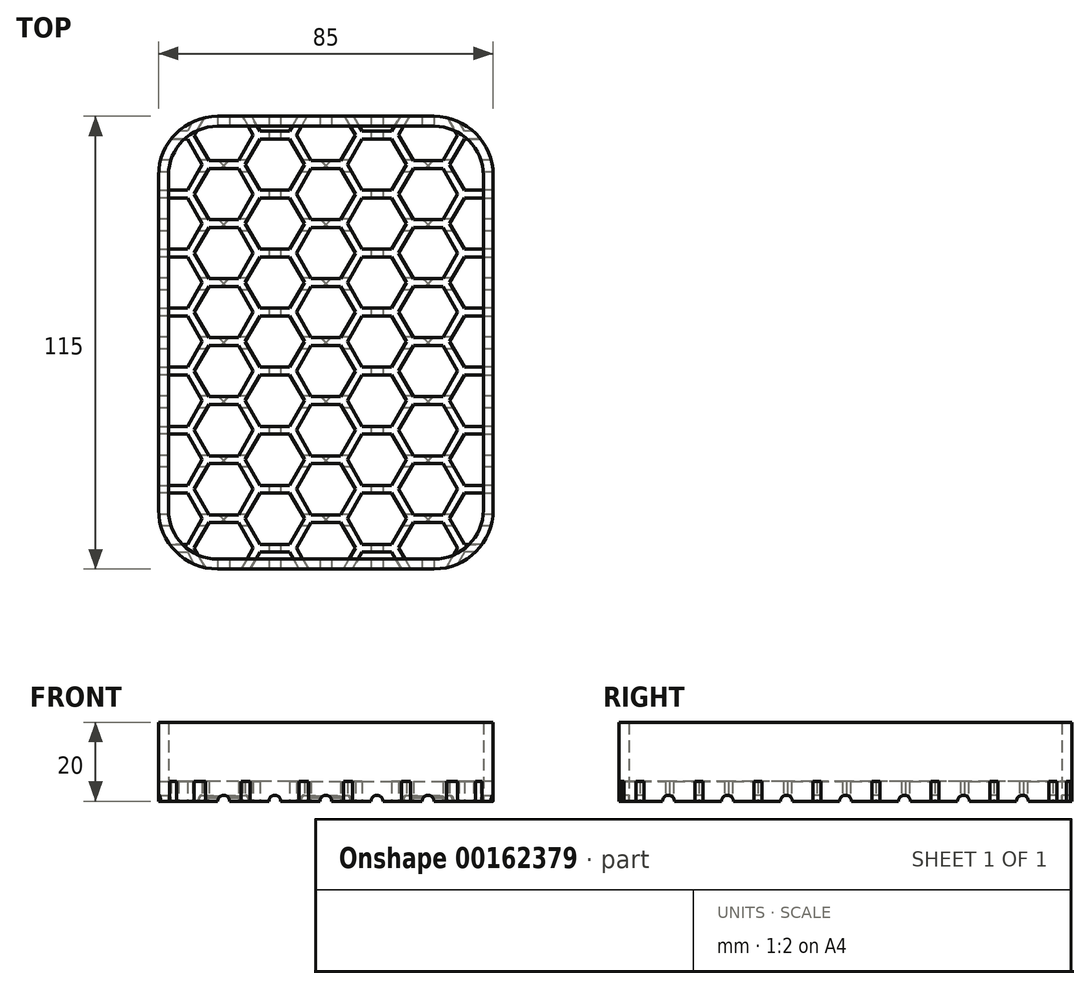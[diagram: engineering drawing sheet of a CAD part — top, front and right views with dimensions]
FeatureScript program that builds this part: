
annotation { "Feature Type Name" : "Feature", "Feature Type Description" : "" }
export const myFeature = defineFeature(function(context is Context, id is Id, definition is map)
    precondition{}
    {
        {
            var Q0;
            Q0=qCreatedBy(makeId("Top.planeOp"),FACE);
            var sketch = newSketch(context, id + "F0", { "sketchPlane" : qUnion([Q0])});
            skLineSegment(sketch, "E0.bottom", {"start": v(27.5, 57.5) * mm, "end": v(-27.5, 57.5) * mm});
            skLineSegment(sketch, "E0.top", {"start": v(27.5, -57.5) * mm, "end": v(-27.5, -57.5) * mm});
            skLineSegment(sketch, "E0.left", {"start": v(42.5, 42.5) * mm, "end": v(42.5, -42.5) * mm});
            skLineSegment(sketch, "E0.right", {"start": v(-42.5, 42.5) * mm, "end": v(-42.5, -42.5) * mm});
            skPoint(sketch, "E0.middle", {"position": v(0, 0) * mm});
            skArc(sketch, "E1", {"start": v(-27.5, 57.5) * mm, "mid": v(-38.1, 53.1) * mm, "end": v(-42.5, 42.5) * mm});
            skArc(sketch, "E2", {"start": v(42.5, 42.5) * mm, "mid": v(38.1, 53.1) * mm, "end": v(27.5, 57.5) * mm});
            skArc(sketch, "E3", {"start": v(27.5, -57.5) * mm, "mid": v(38.1, -53.1) * mm, "end": v(42.5, -42.5) * mm});
            skArc(sketch, "E4", {"start": v(-42.5, -42.5) * mm, "mid": v(-38.1, -53.1) * mm, "end": v(-27.5, -57.5) * mm});
            skSolve(sketch);
        }
        {
            var Q0;
            Q0=makeQuery(id+"F0.imprint","IMPRINT",FACE,{"disambiguationData":[TD([[makeQuery(id+"F0.imprint","IMPRINT",EDGE,{"derivedFrom":sQuery(id+"F0.wireOp",EDGE,"E0.bottom")}),1.0]])]});
            extrude(context, id + "F1", {"entities" : qUnion([Q0]), "depth" : 5 * mm});
        }
        {
            var Q0;
            Q0=qCreatedBy(makeId("Top.planeOp"),FACE);
            var sketch = newSketch(context, id + "F2", { "sketchPlane" : qUnion([Q0])});
            skCircle(sketch, "E5.cCircle", {"center": v(0, -52.22) * mm, "radius": 7.5 * mm, "construction": true});
            skLineSegment(sketch, "E5.0", {"start": v(7.5, -52.22) * mm, "end": v(3.75, -58.72) * mm});
            skLineSegment(sketch, "E5.1", {"start": v(3.75, -58.72) * mm, "end": v(-3.75, -58.72) * mm});
            skLineSegment(sketch, "E5.2", {"start": v(-3.75, -58.72) * mm, "end": v(-7.5, -52.22) * mm});
            skLineSegment(sketch, "E5.3", {"start": v(-7.5, -52.22) * mm, "end": v(-3.75, -45.73) * mm});
            skLineSegment(sketch, "E5.4", {"start": v(-3.75, -45.73) * mm, "end": v(3.75, -45.73) * mm});
            skLineSegment(sketch, "E5.5", {"start": v(3.75, -45.73) * mm, "end": v(7.5, -52.22) * mm});
            skCircle(sketch, "E6.cCircle", {"center": v(-12.98, -59.72) * mm, "radius": 7.5 * mm, "construction": true});
            skLineSegment(sketch, "E6.0", {"start": v(-16.73, -53.22) * mm, "end": v(-9.23, -53.22) * mm});
            skLineSegment(sketch, "E6.1", {"start": v(-9.23, -53.22) * mm, "end": v(-5.48, -59.72) * mm});
            skLineSegment(sketch, "E6.2", {"start": v(-5.48, -59.72) * mm, "end": v(-9.23, -66.21) * mm});
            skLineSegment(sketch, "E6.3", {"start": v(-9.23, -66.21) * mm, "end": v(-16.73, -66.21) * mm});
            skLineSegment(sketch, "E6.4", {"start": v(-16.73, -66.21) * mm, "end": v(-20.48, -59.72) * mm});
            skLineSegment(sketch, "E6.5", {"start": v(-20.48, -59.72) * mm, "end": v(-16.73, -53.22) * mm});
            skLineSegment(sketch, "E7", {"start": v(-12.98, -59.72) * mm, "end": v(0, -52.22) * mm, "construction": true});
            skCircle(sketch, "E8.MirrorC", {"center": v(12.98, -59.72) * mm, "radius": 7.5 * mm, "construction": true});
            skLineSegment(sketch, "E9.MirrorCS", {"start": v(5.48, -59.72) * mm, "end": v(9.23, -66.21) * mm});
            skLineSegment(sketch, "E10.MirrorCS", {"start": v(9.23, -66.21) * mm, "end": v(16.73, -66.21) * mm});
            skLineSegment(sketch, "E11.MirrorCS", {"start": v(16.73, -66.21) * mm, "end": v(20.48, -59.72) * mm});
            skLineSegment(sketch, "E12.MirrorCS", {"start": v(20.48, -59.72) * mm, "end": v(16.73, -53.22) * mm});
            skLineSegment(sketch, "E13.MirrorCS", {"start": v(16.73, -53.22) * mm, "end": v(9.23, -53.22) * mm});
            skLineSegment(sketch, "E14.MirrorCS", {"start": v(9.23, -53.22) * mm, "end": v(5.48, -59.72) * mm});
            skLineSegment(sketch, "E15.MirrorCS", {"start": v(12.98, -59.72) * mm, "end": v(0, -52.22) * mm, "construction": true});
            skLineSegment(sketch, "E16.1.0.0", {"start": v(38.95, -59.72) * mm, "end": v(25.96, -52.22) * mm, "construction": true});
            skLineSegment(sketch, "E16.1.0.1", {"start": v(29.71, -45.73) * mm, "end": v(33.46, -52.22) * mm});
            skLineSegment(sketch, "E16.1.0.2", {"start": v(12.98, -59.72) * mm, "end": v(25.96, -52.22) * mm, "construction": true});
            skLineSegment(sketch, "E16.1.0.3", {"start": v(22.21, -45.73) * mm, "end": v(29.71, -45.73) * mm});
            skLineSegment(sketch, "E16.1.0.4", {"start": v(42.7, -66.21) * mm, "end": v(46.45, -59.72) * mm});
            skLineSegment(sketch, "E16.1.0.5", {"start": v(46.45, -59.72) * mm, "end": v(42.7, -53.22) * mm});
            skLineSegment(sketch, "E16.1.0.6", {"start": v(31.45, -59.72) * mm, "end": v(35.2, -66.21) * mm});
            skCircle(sketch, "E16.1.0.7", {"center": v(25.96, -52.22) * mm, "radius": 7.5 * mm, "construction": true});
            skLineSegment(sketch, "E16.1.0.8", {"start": v(35.2, -53.22) * mm, "end": v(31.45, -59.72) * mm});
            skLineSegment(sketch, "E16.1.0.9", {"start": v(33.46, -52.22) * mm, "end": v(29.71, -58.72) * mm});
            skLineSegment(sketch, "E16.1.0.10", {"start": v(35.2, -66.21) * mm, "end": v(42.7, -66.21) * mm});
            skLineSegment(sketch, "E16.1.0.11", {"start": v(29.71, -58.72) * mm, "end": v(22.21, -58.72) * mm});
            skLineSegment(sketch, "E16.1.0.12", {"start": v(22.21, -58.72) * mm, "end": v(18.46, -52.22) * mm});
            skLineSegment(sketch, "E16.1.0.13", {"start": v(42.7, -53.22) * mm, "end": v(35.2, -53.22) * mm});
            skLineSegment(sketch, "E16.1.0.14", {"start": v(18.46, -52.22) * mm, "end": v(22.21, -45.73) * mm});
            skCircle(sketch, "E16.1.0.15", {"center": v(38.95, -59.72) * mm, "radius": 7.5 * mm, "construction": true});
            skLineSegment(sketch, "E16.direction1", {"start": v(-12.98, -59.72) * mm, "end": v(12.98, -59.72) * mm, "construction": true});
            skCircle(sketch, "E17.MirrorC", {"center": v(-25.96, -52.22) * mm, "radius": 7.5 * mm, "construction": true});
            skLineSegment(sketch, "E18.MirrorCS", {"start": v(-35.2, -66.21) * mm, "end": v(-42.7, -66.21) * mm});
            skLineSegment(sketch, "E19.MirrorCS", {"start": v(-12.98, -59.72) * mm, "end": v(-25.96, -52.22) * mm, "construction": true});
            skLineSegment(sketch, "E20.MirrorCS", {"start": v(-38.95, -59.72) * mm, "end": v(-25.96, -52.22) * mm, "construction": true});
            skLineSegment(sketch, "E21.MirrorCS", {"start": v(-46.45, -59.72) * mm, "end": v(-42.7, -53.22) * mm});
            skCircle(sketch, "E22.MirrorC", {"center": v(-38.95, -59.72) * mm, "radius": 7.5 * mm, "construction": true});
            skLineSegment(sketch, "E23.MirrorCS", {"start": v(-35.2, -53.22) * mm, "end": v(-31.45, -59.72) * mm});
            skLineSegment(sketch, "E24.MirrorCS", {"start": v(-29.71, -58.72) * mm, "end": v(-22.21, -58.72) * mm});
            skLineSegment(sketch, "E25.MirrorCS", {"start": v(-22.21, -45.73) * mm, "end": v(-29.71, -45.73) * mm});
            skLineSegment(sketch, "E26.MirrorCS", {"start": v(-22.21, -58.72) * mm, "end": v(-18.46, -52.22) * mm});
            skLineSegment(sketch, "E27.MirrorCS", {"start": v(-18.46, -52.22) * mm, "end": v(-22.21, -45.73) * mm});
            skLineSegment(sketch, "E28.MirrorCS", {"start": v(-31.45, -59.72) * mm, "end": v(-35.2, -66.21) * mm});
            skLineSegment(sketch, "E29.MirrorCS", {"start": v(-42.7, -66.21) * mm, "end": v(-46.45, -59.72) * mm});
            skLineSegment(sketch, "E30.MirrorCS", {"start": v(-33.46, -52.22) * mm, "end": v(-29.71, -58.72) * mm});
            skLineSegment(sketch, "E31.MirrorCS", {"start": v(-29.71, -45.73) * mm, "end": v(-33.46, -52.22) * mm});
            skLineSegment(sketch, "E32.MirrorCS", {"start": v(-42.7, -53.22) * mm, "end": v(-35.2, -53.22) * mm});
            skLineSegment(sketch, "E33.0.1.0", {"start": v(-3.75, -30.74) * mm, "end": v(3.75, -30.74) * mm});
            skLineSegment(sketch, "E33.0.1.1", {"start": v(-7.5, -37.23) * mm, "end": v(-3.75, -30.74) * mm});
            skLineSegment(sketch, "E33.0.1.2", {"start": v(7.5, -37.23) * mm, "end": v(3.75, -43.73) * mm});
            skLineSegment(sketch, "E33.0.1.3", {"start": v(-20.48, -44.73) * mm, "end": v(-16.73, -38.23) * mm});
            skCircle(sketch, "E33.0.1.4", {"center": v(-25.96, -37.23) * mm, "radius": 7.5 * mm, "construction": true});
            skLineSegment(sketch, "E33.0.1.5", {"start": v(35.2, -38.23) * mm, "end": v(31.45, -44.73) * mm});
            skLineSegment(sketch, "E33.0.1.6", {"start": v(12.98, -44.73) * mm, "end": v(0, -37.23) * mm, "construction": true});
            skCircle(sketch, "E33.0.1.7", {"center": v(38.95, -44.73) * mm, "radius": 7.5 * mm, "construction": true});
            skLineSegment(sketch, "E33.0.1.8", {"start": v(-12.98, -44.73) * mm, "end": v(0, -37.23) * mm, "construction": true});
            skLineSegment(sketch, "E33.0.1.9", {"start": v(9.23, -38.23) * mm, "end": v(5.48, -44.73) * mm});
            skCircle(sketch, "E33.0.1.10", {"center": v(-38.95, -44.73) * mm, "radius": 7.5 * mm, "construction": true});
            skLineSegment(sketch, "E33.0.1.11", {"start": v(-5.48, -44.73) * mm, "end": v(-9.23, -51.22) * mm});
            skLineSegment(sketch, "E33.0.1.12", {"start": v(33.46, -37.23) * mm, "end": v(29.71, -43.73) * mm});
            skLineSegment(sketch, "E33.0.1.13", {"start": v(35.2, -51.22) * mm, "end": v(42.7, -51.22) * mm});
            skLineSegment(sketch, "E33.0.1.14", {"start": v(29.71, -43.73) * mm, "end": v(22.21, -43.73) * mm});
            skLineSegment(sketch, "E33.0.1.15", {"start": v(12.98, -44.73) * mm, "end": v(25.96, -37.23) * mm, "construction": true});
            skCircle(sketch, "E33.0.1.16", {"center": v(0, -37.23) * mm, "radius": 7.5 * mm, "construction": true});
            skCircle(sketch, "E33.0.1.17", {"center": v(-12.98, -44.73) * mm, "radius": 7.5 * mm, "construction": true});
            skLineSegment(sketch, "E33.0.1.18", {"start": v(-16.73, -38.23) * mm, "end": v(-9.23, -38.23) * mm});
            skLineSegment(sketch, "E33.0.1.19", {"start": v(-3.75, -43.73) * mm, "end": v(-7.5, -37.23) * mm});
            skLineSegment(sketch, "E33.0.1.20", {"start": v(3.75, -30.74) * mm, "end": v(7.5, -37.23) * mm});
            skLineSegment(sketch, "E33.0.1.21", {"start": v(-22.21, -43.73) * mm, "end": v(-18.46, -37.23) * mm});
            skLineSegment(sketch, "E33.0.1.22", {"start": v(-31.45, -44.73) * mm, "end": v(-35.2, -51.22) * mm});
            skLineSegment(sketch, "E33.0.1.23", {"start": v(16.73, -38.23) * mm, "end": v(9.23, -38.23) * mm});
            skLineSegment(sketch, "E33.0.1.24", {"start": v(29.71, -30.74) * mm, "end": v(33.46, -37.23) * mm});
            skLineSegment(sketch, "E33.0.1.25", {"start": v(46.45, -44.73) * mm, "end": v(42.7, -38.23) * mm});
            skLineSegment(sketch, "E33.0.1.26", {"start": v(42.7, -51.22) * mm, "end": v(46.45, -44.73) * mm});
            skLineSegment(sketch, "E33.0.1.27", {"start": v(5.48, -44.73) * mm, "end": v(9.23, -51.22) * mm});
            skLineSegment(sketch, "E33.0.1.28", {"start": v(-46.45, -44.73) * mm, "end": v(-42.7, -38.23) * mm});
            skLineSegment(sketch, "E33.0.1.29", {"start": v(31.45, -44.73) * mm, "end": v(35.2, -51.22) * mm});
            skLineSegment(sketch, "E33.0.1.30", {"start": v(16.73, -51.22) * mm, "end": v(20.48, -44.73) * mm});
            skLineSegment(sketch, "E33.0.1.31", {"start": v(-16.73, -51.22) * mm, "end": v(-20.48, -44.73) * mm});
            skLineSegment(sketch, "E33.0.1.32", {"start": v(-29.71, -43.73) * mm, "end": v(-22.21, -43.73) * mm});
            skLineSegment(sketch, "E33.0.1.33", {"start": v(20.48, -44.73) * mm, "end": v(16.73, -38.23) * mm});
            skLineSegment(sketch, "E33.0.1.34", {"start": v(-12.98, -44.73) * mm, "end": v(-25.96, -37.23) * mm, "construction": true});
            skLineSegment(sketch, "E33.0.1.35", {"start": v(-18.46, -37.23) * mm, "end": v(-22.21, -30.74) * mm});
            skLineSegment(sketch, "E33.0.1.36", {"start": v(42.7, -38.23) * mm, "end": v(35.2, -38.23) * mm});
            skLineSegment(sketch, "E33.0.1.37", {"start": v(-22.21, -30.74) * mm, "end": v(-29.71, -30.74) * mm});
            skLineSegment(sketch, "E33.0.1.38", {"start": v(-35.2, -38.23) * mm, "end": v(-31.45, -44.73) * mm});
            skLineSegment(sketch, "E33.0.1.39", {"start": v(-9.23, -51.22) * mm, "end": v(-16.73, -51.22) * mm});
            skLineSegment(sketch, "E33.0.1.40", {"start": v(22.21, -30.74) * mm, "end": v(29.71, -30.74) * mm});
            skLineSegment(sketch, "E33.0.1.41", {"start": v(22.21, -43.73) * mm, "end": v(18.46, -37.23) * mm});
            skLineSegment(sketch, "E33.0.1.42", {"start": v(3.75, -43.73) * mm, "end": v(-3.75, -43.73) * mm});
            skLineSegment(sketch, "E33.0.1.43", {"start": v(38.95, -44.73) * mm, "end": v(25.96, -37.23) * mm, "construction": true});
            skCircle(sketch, "E33.0.1.44", {"center": v(12.98, -44.73) * mm, "radius": 7.5 * mm, "construction": true});
            skLineSegment(sketch, "E33.0.1.45", {"start": v(-29.71, -30.74) * mm, "end": v(-33.46, -37.23) * mm});
            skCircle(sketch, "E33.0.1.46", {"center": v(25.96, -37.23) * mm, "radius": 7.5 * mm, "construction": true});
            skLineSegment(sketch, "E33.0.1.47", {"start": v(18.46, -37.23) * mm, "end": v(22.21, -30.74) * mm});
            skLineSegment(sketch, "E33.0.1.48", {"start": v(-35.2, -51.22) * mm, "end": v(-42.7, -51.22) * mm});
            skLineSegment(sketch, "E33.0.1.49", {"start": v(9.23, -51.22) * mm, "end": v(16.73, -51.22) * mm});
            skLineSegment(sketch, "E33.0.1.50", {"start": v(-33.46, -37.23) * mm, "end": v(-29.71, -43.73) * mm});
            skLineSegment(sketch, "E33.0.1.51", {"start": v(-42.7, -38.23) * mm, "end": v(-35.2, -38.23) * mm});
            skLineSegment(sketch, "E33.0.1.52", {"start": v(-42.7, -51.22) * mm, "end": v(-46.45, -44.73) * mm});
            skLineSegment(sketch, "E33.0.1.53", {"start": v(-38.95, -44.73) * mm, "end": v(-25.96, -37.23) * mm, "construction": true});
            skLineSegment(sketch, "E33.0.1.54", {"start": v(-12.98, -44.73) * mm, "end": v(12.98, -44.73) * mm, "construction": true});
            skLineSegment(sketch, "E33.0.1.55", {"start": v(-9.23, -38.23) * mm, "end": v(-5.48, -44.73) * mm});
            skLineSegment(sketch, "E33.0.2.0", {"start": v(-3.75, -15.75) * mm, "end": v(3.75, -15.75) * mm});
            skLineSegment(sketch, "E33.0.2.1", {"start": v(-7.5, -22.24) * mm, "end": v(-3.75, -15.75) * mm});
            skLineSegment(sketch, "E33.0.2.2", {"start": v(7.5, -22.24) * mm, "end": v(3.75, -28.74) * mm});
            skLineSegment(sketch, "E33.0.2.3", {"start": v(-20.48, -29.74) * mm, "end": v(-16.73, -23.24) * mm});
            skCircle(sketch, "E33.0.2.4", {"center": v(-25.96, -22.24) * mm, "radius": 7.5 * mm, "construction": true});
            skLineSegment(sketch, "E33.0.2.5", {"start": v(35.2, -23.24) * mm, "end": v(31.45, -29.74) * mm});
            skLineSegment(sketch, "E33.0.2.6", {"start": v(12.98, -29.74) * mm, "end": v(0, -22.24) * mm, "construction": true});
            skCircle(sketch, "E33.0.2.7", {"center": v(38.95, -29.74) * mm, "radius": 7.5 * mm, "construction": true});
            skLineSegment(sketch, "E33.0.2.8", {"start": v(-12.98, -29.74) * mm, "end": v(0, -22.24) * mm, "construction": true});
            skLineSegment(sketch, "E33.0.2.9", {"start": v(9.23, -23.24) * mm, "end": v(5.48, -29.74) * mm});
            skCircle(sketch, "E33.0.2.10", {"center": v(-38.95, -29.74) * mm, "radius": 7.5 * mm, "construction": true});
            skLineSegment(sketch, "E33.0.2.11", {"start": v(-5.48, -29.74) * mm, "end": v(-9.23, -36.23) * mm});
            skLineSegment(sketch, "E33.0.2.12", {"start": v(33.46, -22.24) * mm, "end": v(29.71, -28.74) * mm});
            skLineSegment(sketch, "E33.0.2.13", {"start": v(35.2, -36.23) * mm, "end": v(42.7, -36.23) * mm});
            skLineSegment(sketch, "E33.0.2.14", {"start": v(29.71, -28.74) * mm, "end": v(22.21, -28.74) * mm});
            skLineSegment(sketch, "E33.0.2.15", {"start": v(12.98, -29.74) * mm, "end": v(25.96, -22.24) * mm, "construction": true});
            skCircle(sketch, "E33.0.2.16", {"center": v(0, -22.24) * mm, "radius": 7.5 * mm, "construction": true});
            skCircle(sketch, "E33.0.2.17", {"center": v(-12.98, -29.74) * mm, "radius": 7.5 * mm, "construction": true});
            skLineSegment(sketch, "E33.0.2.18", {"start": v(-16.73, -23.24) * mm, "end": v(-9.23, -23.24) * mm});
            skLineSegment(sketch, "E33.0.2.19", {"start": v(-3.75, -28.74) * mm, "end": v(-7.5, -22.24) * mm});
            skLineSegment(sketch, "E33.0.2.20", {"start": v(3.75, -15.75) * mm, "end": v(7.5, -22.24) * mm});
            skLineSegment(sketch, "E33.0.2.21", {"start": v(-22.21, -28.74) * mm, "end": v(-18.46, -22.24) * mm});
            skLineSegment(sketch, "E33.0.2.22", {"start": v(-31.45, -29.74) * mm, "end": v(-35.2, -36.23) * mm});
            skLineSegment(sketch, "E33.0.2.23", {"start": v(16.73, -23.24) * mm, "end": v(9.23, -23.24) * mm});
            skLineSegment(sketch, "E33.0.2.24", {"start": v(29.71, -15.75) * mm, "end": v(33.46, -22.24) * mm});
            skLineSegment(sketch, "E33.0.2.25", {"start": v(46.45, -29.74) * mm, "end": v(42.7, -23.24) * mm});
            skLineSegment(sketch, "E33.0.2.26", {"start": v(42.7, -36.23) * mm, "end": v(46.45, -29.74) * mm});
            skLineSegment(sketch, "E33.0.2.27", {"start": v(5.48, -29.74) * mm, "end": v(9.23, -36.23) * mm});
            skLineSegment(sketch, "E33.0.2.28", {"start": v(-46.45, -29.74) * mm, "end": v(-42.7, -23.24) * mm});
            skLineSegment(sketch, "E33.0.2.29", {"start": v(31.45, -29.74) * mm, "end": v(35.2, -36.23) * mm});
            skLineSegment(sketch, "E33.0.2.30", {"start": v(16.73, -36.23) * mm, "end": v(20.48, -29.74) * mm});
            skLineSegment(sketch, "E33.0.2.31", {"start": v(-16.73, -36.23) * mm, "end": v(-20.48, -29.74) * mm});
            skLineSegment(sketch, "E33.0.2.32", {"start": v(-29.71, -28.74) * mm, "end": v(-22.21, -28.74) * mm});
            skLineSegment(sketch, "E33.0.2.33", {"start": v(20.48, -29.74) * mm, "end": v(16.73, -23.24) * mm});
            skLineSegment(sketch, "E33.0.2.34", {"start": v(-12.98, -29.74) * mm, "end": v(-25.96, -22.24) * mm, "construction": true});
            skLineSegment(sketch, "E33.0.2.35", {"start": v(-18.46, -22.24) * mm, "end": v(-22.21, -15.75) * mm});
            skLineSegment(sketch, "E33.0.2.36", {"start": v(42.7, -23.24) * mm, "end": v(35.2, -23.24) * mm});
            skLineSegment(sketch, "E33.0.2.37", {"start": v(-22.21, -15.75) * mm, "end": v(-29.71, -15.75) * mm});
            skLineSegment(sketch, "E33.0.2.38", {"start": v(-35.2, -23.24) * mm, "end": v(-31.45, -29.74) * mm});
            skLineSegment(sketch, "E33.0.2.39", {"start": v(-9.23, -36.23) * mm, "end": v(-16.73, -36.23) * mm});
            skLineSegment(sketch, "E33.0.2.40", {"start": v(22.21, -15.75) * mm, "end": v(29.71, -15.75) * mm});
            skLineSegment(sketch, "E33.0.2.41", {"start": v(22.21, -28.74) * mm, "end": v(18.46, -22.24) * mm});
            skLineSegment(sketch, "E33.0.2.42", {"start": v(3.75, -28.74) * mm, "end": v(-3.75, -28.74) * mm});
            skLineSegment(sketch, "E33.0.2.43", {"start": v(38.95, -29.74) * mm, "end": v(25.96, -22.24) * mm, "construction": true});
            skCircle(sketch, "E33.0.2.44", {"center": v(12.98, -29.74) * mm, "radius": 7.5 * mm, "construction": true});
            skLineSegment(sketch, "E33.0.2.45", {"start": v(-29.71, -15.75) * mm, "end": v(-33.46, -22.24) * mm});
            skCircle(sketch, "E33.0.2.46", {"center": v(25.96, -22.24) * mm, "radius": 7.5 * mm, "construction": true});
            skLineSegment(sketch, "E33.0.2.47", {"start": v(18.46, -22.24) * mm, "end": v(22.21, -15.75) * mm});
            skLineSegment(sketch, "E33.0.2.48", {"start": v(-35.2, -36.23) * mm, "end": v(-42.7, -36.23) * mm});
            skLineSegment(sketch, "E33.0.2.49", {"start": v(9.23, -36.23) * mm, "end": v(16.73, -36.23) * mm});
            skLineSegment(sketch, "E33.0.2.50", {"start": v(-33.46, -22.24) * mm, "end": v(-29.71, -28.74) * mm});
            skLineSegment(sketch, "E33.0.2.51", {"start": v(-42.7, -23.24) * mm, "end": v(-35.2, -23.24) * mm});
            skLineSegment(sketch, "E33.0.2.52", {"start": v(-42.7, -36.23) * mm, "end": v(-46.45, -29.74) * mm});
            skLineSegment(sketch, "E33.0.2.53", {"start": v(-38.95, -29.74) * mm, "end": v(-25.96, -22.24) * mm, "construction": true});
            skLineSegment(sketch, "E33.0.2.54", {"start": v(-12.98, -29.74) * mm, "end": v(12.98, -29.74) * mm, "construction": true});
            skLineSegment(sketch, "E33.0.2.55", {"start": v(-9.23, -23.24) * mm, "end": v(-5.48, -29.74) * mm});
            skLineSegment(sketch, "E33.0.3.0", {"start": v(-3.75, -0.76) * mm, "end": v(3.75, -0.76) * mm});
            skLineSegment(sketch, "E33.0.3.1", {"start": v(-7.5, -7.25) * mm, "end": v(-3.75, -0.76) * mm});
            skLineSegment(sketch, "E33.0.3.2", {"start": v(7.5, -7.25) * mm, "end": v(3.75, -13.75) * mm});
            skLineSegment(sketch, "E33.0.3.3", {"start": v(-20.48, -14.75) * mm, "end": v(-16.73, -8.25) * mm});
            skCircle(sketch, "E33.0.3.4", {"center": v(-25.96, -7.25) * mm, "radius": 7.5 * mm, "construction": true});
            skLineSegment(sketch, "E33.0.3.5", {"start": v(35.2, -8.25) * mm, "end": v(31.45, -14.75) * mm});
            skLineSegment(sketch, "E33.0.3.6", {"start": v(12.98, -14.75) * mm, "end": v(0, -7.25) * mm, "construction": true});
            skCircle(sketch, "E33.0.3.7", {"center": v(38.95, -14.75) * mm, "radius": 7.5 * mm, "construction": true});
            skLineSegment(sketch, "E33.0.3.8", {"start": v(-12.98, -14.75) * mm, "end": v(0, -7.25) * mm, "construction": true});
            skLineSegment(sketch, "E33.0.3.9", {"start": v(9.23, -8.25) * mm, "end": v(5.48, -14.75) * mm});
            skCircle(sketch, "E33.0.3.10", {"center": v(-38.95, -14.75) * mm, "radius": 7.5 * mm, "construction": true});
            skLineSegment(sketch, "E33.0.3.11", {"start": v(-5.48, -14.75) * mm, "end": v(-9.23, -21.24) * mm});
            skLineSegment(sketch, "E33.0.3.12", {"start": v(33.46, -7.25) * mm, "end": v(29.71, -13.75) * mm});
            skLineSegment(sketch, "E33.0.3.13", {"start": v(35.2, -21.24) * mm, "end": v(42.7, -21.24) * mm});
            skLineSegment(sketch, "E33.0.3.14", {"start": v(29.71, -13.75) * mm, "end": v(22.21, -13.75) * mm});
            skLineSegment(sketch, "E33.0.3.15", {"start": v(12.98, -14.75) * mm, "end": v(25.96, -7.25) * mm, "construction": true});
            skCircle(sketch, "E33.0.3.16", {"center": v(0, -7.25) * mm, "radius": 7.5 * mm, "construction": true});
            skCircle(sketch, "E33.0.3.17", {"center": v(-12.98, -14.75) * mm, "radius": 7.5 * mm, "construction": true});
            skLineSegment(sketch, "E33.0.3.18", {"start": v(-16.73, -8.25) * mm, "end": v(-9.23, -8.25) * mm});
            skLineSegment(sketch, "E33.0.3.19", {"start": v(-3.75, -13.75) * mm, "end": v(-7.5, -7.25) * mm});
            skLineSegment(sketch, "E33.0.3.20", {"start": v(3.75, -0.76) * mm, "end": v(7.5, -7.25) * mm});
            skLineSegment(sketch, "E33.0.3.21", {"start": v(-22.21, -13.75) * mm, "end": v(-18.46, -7.25) * mm});
            skLineSegment(sketch, "E33.0.3.22", {"start": v(-31.45, -14.75) * mm, "end": v(-35.2, -21.24) * mm});
            skLineSegment(sketch, "E33.0.3.23", {"start": v(16.73, -8.25) * mm, "end": v(9.23, -8.25) * mm});
            skLineSegment(sketch, "E33.0.3.24", {"start": v(29.71, -0.76) * mm, "end": v(33.46, -7.25) * mm});
            skLineSegment(sketch, "E33.0.3.25", {"start": v(46.45, -14.75) * mm, "end": v(42.7, -8.25) * mm});
            skLineSegment(sketch, "E33.0.3.26", {"start": v(42.7, -21.24) * mm, "end": v(46.45, -14.75) * mm});
            skLineSegment(sketch, "E33.0.3.27", {"start": v(5.48, -14.75) * mm, "end": v(9.23, -21.24) * mm});
            skLineSegment(sketch, "E33.0.3.28", {"start": v(-46.45, -14.75) * mm, "end": v(-42.7, -8.25) * mm});
            skLineSegment(sketch, "E33.0.3.29", {"start": v(31.45, -14.75) * mm, "end": v(35.2, -21.24) * mm});
            skLineSegment(sketch, "E33.0.3.30", {"start": v(16.73, -21.24) * mm, "end": v(20.48, -14.75) * mm});
            skLineSegment(sketch, "E33.0.3.31", {"start": v(-16.73, -21.24) * mm, "end": v(-20.48, -14.75) * mm});
            skLineSegment(sketch, "E33.0.3.32", {"start": v(-29.71, -13.75) * mm, "end": v(-22.21, -13.75) * mm});
            skLineSegment(sketch, "E33.0.3.33", {"start": v(20.48, -14.75) * mm, "end": v(16.73, -8.25) * mm});
            skLineSegment(sketch, "E33.0.3.34", {"start": v(-12.98, -14.75) * mm, "end": v(-25.96, -7.25) * mm, "construction": true});
            skLineSegment(sketch, "E33.0.3.35", {"start": v(-18.46, -7.25) * mm, "end": v(-22.21, -0.76) * mm});
            skLineSegment(sketch, "E33.0.3.36", {"start": v(42.7, -8.25) * mm, "end": v(35.2, -8.25) * mm});
            skLineSegment(sketch, "E33.0.3.37", {"start": v(-22.21, -0.76) * mm, "end": v(-29.71, -0.76) * mm});
            skLineSegment(sketch, "E33.0.3.38", {"start": v(-35.2, -8.25) * mm, "end": v(-31.45, -14.75) * mm});
            skLineSegment(sketch, "E33.0.3.39", {"start": v(-9.23, -21.24) * mm, "end": v(-16.73, -21.24) * mm});
            skLineSegment(sketch, "E33.0.3.40", {"start": v(22.21, -0.76) * mm, "end": v(29.71, -0.76) * mm});
            skLineSegment(sketch, "E33.0.3.41", {"start": v(22.21, -13.75) * mm, "end": v(18.46, -7.25) * mm});
            skLineSegment(sketch, "E33.0.3.42", {"start": v(3.75, -13.75) * mm, "end": v(-3.75, -13.75) * mm});
            skLineSegment(sketch, "E33.0.3.43", {"start": v(38.95, -14.75) * mm, "end": v(25.96, -7.25) * mm, "construction": true});
            skCircle(sketch, "E33.0.3.44", {"center": v(12.98, -14.75) * mm, "radius": 7.5 * mm, "construction": true});
            skLineSegment(sketch, "E33.0.3.45", {"start": v(-29.71, -0.76) * mm, "end": v(-33.46, -7.25) * mm});
            skCircle(sketch, "E33.0.3.46", {"center": v(25.96, -7.25) * mm, "radius": 7.5 * mm, "construction": true});
            skLineSegment(sketch, "E33.0.3.47", {"start": v(18.46, -7.25) * mm, "end": v(22.21, -0.76) * mm});
            skLineSegment(sketch, "E33.0.3.48", {"start": v(-35.2, -21.24) * mm, "end": v(-42.7, -21.24) * mm});
            skLineSegment(sketch, "E33.0.3.49", {"start": v(9.23, -21.24) * mm, "end": v(16.73, -21.24) * mm});
            skLineSegment(sketch, "E33.0.3.50", {"start": v(-33.46, -7.25) * mm, "end": v(-29.71, -13.75) * mm});
            skLineSegment(sketch, "E33.0.3.51", {"start": v(-42.7, -8.25) * mm, "end": v(-35.2, -8.25) * mm});
            skLineSegment(sketch, "E33.0.3.52", {"start": v(-42.7, -21.24) * mm, "end": v(-46.45, -14.75) * mm});
            skLineSegment(sketch, "E33.0.3.53", {"start": v(-38.95, -14.75) * mm, "end": v(-25.96, -7.25) * mm, "construction": true});
            skLineSegment(sketch, "E33.0.3.54", {"start": v(-12.98, -14.75) * mm, "end": v(12.98, -14.75) * mm, "construction": true});
            skLineSegment(sketch, "E33.0.3.55", {"start": v(-9.23, -8.25) * mm, "end": v(-5.48, -14.75) * mm});
            skLineSegment(sketch, "E33.0.4.0", {"start": v(-3.75, 14.23) * mm, "end": v(3.75, 14.23) * mm});
            skLineSegment(sketch, "E33.0.4.1", {"start": v(-7.5, 7.74) * mm, "end": v(-3.75, 14.23) * mm});
            skLineSegment(sketch, "E33.0.4.2", {"start": v(7.5, 7.74) * mm, "end": v(3.75, 1.24) * mm});
            skLineSegment(sketch, "E33.0.4.3", {"start": v(-20.48, 0.24) * mm, "end": v(-16.73, 6.74) * mm});
            skCircle(sketch, "E33.0.4.4", {"center": v(-25.96, 7.74) * mm, "radius": 7.5 * mm, "construction": true});
            skLineSegment(sketch, "E33.0.4.5", {"start": v(35.2, 6.74) * mm, "end": v(31.45, 0.24) * mm});
            skLineSegment(sketch, "E33.0.4.6", {"start": v(12.98, 0.24) * mm, "end": v(0, 7.74) * mm, "construction": true});
            skCircle(sketch, "E33.0.4.7", {"center": v(38.95, 0.24) * mm, "radius": 7.5 * mm, "construction": true});
            skLineSegment(sketch, "E33.0.4.8", {"start": v(-12.98, 0.24) * mm, "end": v(0, 7.74) * mm, "construction": true});
            skLineSegment(sketch, "E33.0.4.9", {"start": v(9.23, 6.74) * mm, "end": v(5.48, 0.24) * mm});
            skCircle(sketch, "E33.0.4.10", {"center": v(-38.95, 0.24) * mm, "radius": 7.5 * mm, "construction": true});
            skLineSegment(sketch, "E33.0.4.11", {"start": v(-5.48, 0.24) * mm, "end": v(-9.23, -6.25) * mm});
            skLineSegment(sketch, "E33.0.4.12", {"start": v(33.46, 7.74) * mm, "end": v(29.71, 1.24) * mm});
            skLineSegment(sketch, "E33.0.4.13", {"start": v(35.2, -6.25) * mm, "end": v(42.7, -6.25) * mm});
            skLineSegment(sketch, "E33.0.4.14", {"start": v(29.71, 1.24) * mm, "end": v(22.21, 1.24) * mm});
            skLineSegment(sketch, "E33.0.4.15", {"start": v(12.98, 0.24) * mm, "end": v(25.96, 7.74) * mm, "construction": true});
            skCircle(sketch, "E33.0.4.16", {"center": v(0, 7.74) * mm, "radius": 7.5 * mm, "construction": true});
            skCircle(sketch, "E33.0.4.17", {"center": v(-12.98, 0.24) * mm, "radius": 7.5 * mm, "construction": true});
            skLineSegment(sketch, "E33.0.4.18", {"start": v(-16.73, 6.74) * mm, "end": v(-9.23, 6.74) * mm});
            skLineSegment(sketch, "E33.0.4.19", {"start": v(-3.75, 1.24) * mm, "end": v(-7.5, 7.74) * mm});
            skLineSegment(sketch, "E33.0.4.20", {"start": v(3.75, 14.23) * mm, "end": v(7.5, 7.74) * mm});
            skLineSegment(sketch, "E33.0.4.21", {"start": v(-22.21, 1.24) * mm, "end": v(-18.46, 7.74) * mm});
            skLineSegment(sketch, "E33.0.4.22", {"start": v(-31.45, 0.24) * mm, "end": v(-35.2, -6.25) * mm});
            skLineSegment(sketch, "E33.0.4.23", {"start": v(16.73, 6.74) * mm, "end": v(9.23, 6.74) * mm});
            skLineSegment(sketch, "E33.0.4.24", {"start": v(29.71, 14.23) * mm, "end": v(33.46, 7.74) * mm});
            skLineSegment(sketch, "E33.0.4.25", {"start": v(46.45, 0.24) * mm, "end": v(42.7, 6.74) * mm});
            skLineSegment(sketch, "E33.0.4.26", {"start": v(42.7, -6.25) * mm, "end": v(46.45, 0.24) * mm});
            skLineSegment(sketch, "E33.0.4.27", {"start": v(5.48, 0.24) * mm, "end": v(9.23, -6.25) * mm});
            skLineSegment(sketch, "E33.0.4.28", {"start": v(-46.45, 0.24) * mm, "end": v(-42.7, 6.74) * mm});
            skLineSegment(sketch, "E33.0.4.29", {"start": v(31.45, 0.24) * mm, "end": v(35.2, -6.25) * mm});
            skLineSegment(sketch, "E33.0.4.30", {"start": v(16.73, -6.25) * mm, "end": v(20.48, 0.24) * mm});
            skLineSegment(sketch, "E33.0.4.31", {"start": v(-16.73, -6.25) * mm, "end": v(-20.48, 0.24) * mm});
            skLineSegment(sketch, "E33.0.4.32", {"start": v(-29.71, 1.24) * mm, "end": v(-22.21, 1.24) * mm});
            skLineSegment(sketch, "E33.0.4.33", {"start": v(20.48, 0.24) * mm, "end": v(16.73, 6.74) * mm});
            skLineSegment(sketch, "E33.0.4.34", {"start": v(-12.98, 0.24) * mm, "end": v(-25.96, 7.74) * mm, "construction": true});
            skLineSegment(sketch, "E33.0.4.35", {"start": v(-18.46, 7.74) * mm, "end": v(-22.21, 14.23) * mm});
            skLineSegment(sketch, "E33.0.4.36", {"start": v(42.7, 6.74) * mm, "end": v(35.2, 6.74) * mm});
            skLineSegment(sketch, "E33.0.4.37", {"start": v(-22.21, 14.23) * mm, "end": v(-29.71, 14.23) * mm});
            skLineSegment(sketch, "E33.0.4.38", {"start": v(-35.2, 6.74) * mm, "end": v(-31.45, 0.24) * mm});
            skLineSegment(sketch, "E33.0.4.39", {"start": v(-9.23, -6.25) * mm, "end": v(-16.73, -6.25) * mm});
            skLineSegment(sketch, "E33.0.4.40", {"start": v(22.21, 14.23) * mm, "end": v(29.71, 14.23) * mm});
            skLineSegment(sketch, "E33.0.4.41", {"start": v(22.21, 1.24) * mm, "end": v(18.46, 7.74) * mm});
            skLineSegment(sketch, "E33.0.4.42", {"start": v(3.75, 1.24) * mm, "end": v(-3.75, 1.24) * mm});
            skLineSegment(sketch, "E33.0.4.43", {"start": v(38.95, 0.24) * mm, "end": v(25.96, 7.74) * mm, "construction": true});
            skCircle(sketch, "E33.0.4.44", {"center": v(12.98, 0.24) * mm, "radius": 7.5 * mm, "construction": true});
            skLineSegment(sketch, "E33.0.4.45", {"start": v(-29.71, 14.23) * mm, "end": v(-33.46, 7.74) * mm});
            skCircle(sketch, "E33.0.4.46", {"center": v(25.96, 7.74) * mm, "radius": 7.5 * mm, "construction": true});
            skLineSegment(sketch, "E33.0.4.47", {"start": v(18.46, 7.74) * mm, "end": v(22.21, 14.23) * mm});
            skLineSegment(sketch, "E33.0.4.48", {"start": v(-35.2, -6.25) * mm, "end": v(-42.7, -6.25) * mm});
            skLineSegment(sketch, "E33.0.4.49", {"start": v(9.23, -6.25) * mm, "end": v(16.73, -6.25) * mm});
            skLineSegment(sketch, "E33.0.4.50", {"start": v(-33.46, 7.74) * mm, "end": v(-29.71, 1.24) * mm});
            skLineSegment(sketch, "E33.0.4.51", {"start": v(-42.7, 6.74) * mm, "end": v(-35.2, 6.74) * mm});
            skLineSegment(sketch, "E33.0.4.52", {"start": v(-42.7, -6.25) * mm, "end": v(-46.45, 0.24) * mm});
            skLineSegment(sketch, "E33.0.4.53", {"start": v(-38.95, 0.24) * mm, "end": v(-25.96, 7.74) * mm, "construction": true});
            skLineSegment(sketch, "E33.0.4.54", {"start": v(-12.98, 0.24) * mm, "end": v(12.98, 0.24) * mm, "construction": true});
            skLineSegment(sketch, "E33.0.4.55", {"start": v(-9.23, 6.74) * mm, "end": v(-5.48, 0.24) * mm});
            skLineSegment(sketch, "E33.0.5.0", {"start": v(-3.75, 29.22) * mm, "end": v(3.75, 29.22) * mm});
            skLineSegment(sketch, "E33.0.5.1", {"start": v(-7.5, 22.73) * mm, "end": v(-3.75, 29.22) * mm});
            skLineSegment(sketch, "E33.0.5.2", {"start": v(7.5, 22.73) * mm, "end": v(3.75, 16.23) * mm});
            skLineSegment(sketch, "E33.0.5.3", {"start": v(-20.48, 15.23) * mm, "end": v(-16.73, 21.73) * mm});
            skCircle(sketch, "E33.0.5.4", {"center": v(-25.96, 22.73) * mm, "radius": 7.5 * mm, "construction": true});
            skLineSegment(sketch, "E33.0.5.5", {"start": v(35.2, 21.73) * mm, "end": v(31.45, 15.23) * mm});
            skLineSegment(sketch, "E33.0.5.6", {"start": v(12.98, 15.23) * mm, "end": v(0, 22.73) * mm, "construction": true});
            skCircle(sketch, "E33.0.5.7", {"center": v(38.95, 15.23) * mm, "radius": 7.5 * mm, "construction": true});
            skLineSegment(sketch, "E33.0.5.8", {"start": v(-12.98, 15.23) * mm, "end": v(0, 22.73) * mm, "construction": true});
            skLineSegment(sketch, "E33.0.5.9", {"start": v(9.23, 21.73) * mm, "end": v(5.48, 15.23) * mm});
            skCircle(sketch, "E33.0.5.10", {"center": v(-38.95, 15.23) * mm, "radius": 7.5 * mm, "construction": true});
            skLineSegment(sketch, "E33.0.5.11", {"start": v(-5.48, 15.23) * mm, "end": v(-9.23, 8.74) * mm});
            skLineSegment(sketch, "E33.0.5.12", {"start": v(33.46, 22.73) * mm, "end": v(29.71, 16.23) * mm});
            skLineSegment(sketch, "E33.0.5.13", {"start": v(35.2, 8.74) * mm, "end": v(42.7, 8.74) * mm});
            skLineSegment(sketch, "E33.0.5.14", {"start": v(29.71, 16.23) * mm, "end": v(22.21, 16.23) * mm});
            skLineSegment(sketch, "E33.0.5.15", {"start": v(12.98, 15.23) * mm, "end": v(25.96, 22.73) * mm, "construction": true});
            skCircle(sketch, "E33.0.5.16", {"center": v(0, 22.73) * mm, "radius": 7.5 * mm, "construction": true});
            skCircle(sketch, "E33.0.5.17", {"center": v(-12.98, 15.23) * mm, "radius": 7.5 * mm, "construction": true});
            skLineSegment(sketch, "E33.0.5.18", {"start": v(-16.73, 21.73) * mm, "end": v(-9.23, 21.73) * mm});
            skLineSegment(sketch, "E33.0.5.19", {"start": v(-3.75, 16.23) * mm, "end": v(-7.5, 22.73) * mm});
            skLineSegment(sketch, "E33.0.5.20", {"start": v(3.75, 29.22) * mm, "end": v(7.5, 22.73) * mm});
            skLineSegment(sketch, "E33.0.5.21", {"start": v(-22.21, 16.23) * mm, "end": v(-18.46, 22.73) * mm});
            skLineSegment(sketch, "E33.0.5.22", {"start": v(-31.45, 15.23) * mm, "end": v(-35.2, 8.74) * mm});
            skLineSegment(sketch, "E33.0.5.23", {"start": v(16.73, 21.73) * mm, "end": v(9.23, 21.73) * mm});
            skLineSegment(sketch, "E33.0.5.24", {"start": v(29.71, 29.22) * mm, "end": v(33.46, 22.73) * mm});
            skLineSegment(sketch, "E33.0.5.25", {"start": v(46.45, 15.23) * mm, "end": v(42.7, 21.73) * mm});
            skLineSegment(sketch, "E33.0.5.26", {"start": v(42.7, 8.74) * mm, "end": v(46.45, 15.23) * mm});
            skLineSegment(sketch, "E33.0.5.27", {"start": v(5.48, 15.23) * mm, "end": v(9.23, 8.74) * mm});
            skLineSegment(sketch, "E33.0.5.28", {"start": v(-46.45, 15.23) * mm, "end": v(-42.7, 21.73) * mm});
            skLineSegment(sketch, "E33.0.5.29", {"start": v(31.45, 15.23) * mm, "end": v(35.2, 8.74) * mm});
            skLineSegment(sketch, "E33.0.5.30", {"start": v(16.73, 8.74) * mm, "end": v(20.48, 15.23) * mm});
            skLineSegment(sketch, "E33.0.5.31", {"start": v(-16.73, 8.74) * mm, "end": v(-20.48, 15.23) * mm});
            skLineSegment(sketch, "E33.0.5.32", {"start": v(-29.71, 16.23) * mm, "end": v(-22.21, 16.23) * mm});
            skLineSegment(sketch, "E33.0.5.33", {"start": v(20.48, 15.23) * mm, "end": v(16.73, 21.73) * mm});
            skLineSegment(sketch, "E33.0.5.34", {"start": v(-12.98, 15.23) * mm, "end": v(-25.96, 22.73) * mm, "construction": true});
            skLineSegment(sketch, "E33.0.5.35", {"start": v(-18.46, 22.73) * mm, "end": v(-22.21, 29.22) * mm});
            skLineSegment(sketch, "E33.0.5.36", {"start": v(42.7, 21.73) * mm, "end": v(35.2, 21.73) * mm});
            skLineSegment(sketch, "E33.0.5.37", {"start": v(-22.21, 29.22) * mm, "end": v(-29.71, 29.22) * mm});
            skLineSegment(sketch, "E33.0.5.38", {"start": v(-35.2, 21.73) * mm, "end": v(-31.45, 15.23) * mm});
            skLineSegment(sketch, "E33.0.5.39", {"start": v(-9.23, 8.74) * mm, "end": v(-16.73, 8.74) * mm});
            skLineSegment(sketch, "E33.0.5.40", {"start": v(22.21, 29.22) * mm, "end": v(29.71, 29.22) * mm});
            skLineSegment(sketch, "E33.0.5.41", {"start": v(22.21, 16.23) * mm, "end": v(18.46, 22.73) * mm});
            skLineSegment(sketch, "E33.0.5.42", {"start": v(3.75, 16.23) * mm, "end": v(-3.75, 16.23) * mm});
            skLineSegment(sketch, "E33.0.5.43", {"start": v(38.95, 15.23) * mm, "end": v(25.96, 22.73) * mm, "construction": true});
            skCircle(sketch, "E33.0.5.44", {"center": v(12.98, 15.23) * mm, "radius": 7.5 * mm, "construction": true});
            skLineSegment(sketch, "E33.0.5.45", {"start": v(-29.71, 29.22) * mm, "end": v(-33.46, 22.73) * mm});
            skCircle(sketch, "E33.0.5.46", {"center": v(25.96, 22.73) * mm, "radius": 7.5 * mm, "construction": true});
            skLineSegment(sketch, "E33.0.5.47", {"start": v(18.46, 22.73) * mm, "end": v(22.21, 29.22) * mm});
            skLineSegment(sketch, "E33.0.5.48", {"start": v(-35.2, 8.74) * mm, "end": v(-42.7, 8.74) * mm});
            skLineSegment(sketch, "E33.0.5.49", {"start": v(9.23, 8.74) * mm, "end": v(16.73, 8.74) * mm});
            skLineSegment(sketch, "E33.0.5.50", {"start": v(-33.46, 22.73) * mm, "end": v(-29.71, 16.23) * mm});
            skLineSegment(sketch, "E33.0.5.51", {"start": v(-42.7, 21.73) * mm, "end": v(-35.2, 21.73) * mm});
            skLineSegment(sketch, "E33.0.5.52", {"start": v(-42.7, 8.74) * mm, "end": v(-46.45, 15.23) * mm});
            skLineSegment(sketch, "E33.0.5.53", {"start": v(-38.95, 15.23) * mm, "end": v(-25.96, 22.73) * mm, "construction": true});
            skLineSegment(sketch, "E33.0.5.54", {"start": v(-12.98, 15.23) * mm, "end": v(12.98, 15.23) * mm, "construction": true});
            skLineSegment(sketch, "E33.0.5.55", {"start": v(-9.23, 21.73) * mm, "end": v(-5.48, 15.23) * mm});
            skLineSegment(sketch, "E33.0.6.0", {"start": v(-3.75, 44.21) * mm, "end": v(3.75, 44.21) * mm});
            skLineSegment(sketch, "E33.0.6.1", {"start": v(-7.5, 37.72) * mm, "end": v(-3.75, 44.21) * mm});
            skLineSegment(sketch, "E33.0.6.2", {"start": v(7.5, 37.72) * mm, "end": v(3.75, 31.22) * mm});
            skLineSegment(sketch, "E33.0.6.3", {"start": v(-20.48, 30.22) * mm, "end": v(-16.73, 36.72) * mm});
            skCircle(sketch, "E33.0.6.4", {"center": v(-25.96, 37.72) * mm, "radius": 7.5 * mm, "construction": true});
            skLineSegment(sketch, "E33.0.6.5", {"start": v(35.2, 36.72) * mm, "end": v(31.45, 30.22) * mm});
            skLineSegment(sketch, "E33.0.6.6", {"start": v(12.98, 30.22) * mm, "end": v(0, 37.72) * mm, "construction": true});
            skCircle(sketch, "E33.0.6.7", {"center": v(38.95, 30.22) * mm, "radius": 7.5 * mm, "construction": true});
            skLineSegment(sketch, "E33.0.6.8", {"start": v(-12.98, 30.22) * mm, "end": v(0, 37.72) * mm, "construction": true});
            skLineSegment(sketch, "E33.0.6.9", {"start": v(9.23, 36.72) * mm, "end": v(5.48, 30.22) * mm});
            skCircle(sketch, "E33.0.6.10", {"center": v(-38.95, 30.22) * mm, "radius": 7.5 * mm, "construction": true});
            skLineSegment(sketch, "E33.0.6.11", {"start": v(-5.48, 30.22) * mm, "end": v(-9.23, 23.73) * mm});
            skLineSegment(sketch, "E33.0.6.12", {"start": v(33.46, 37.72) * mm, "end": v(29.71, 31.22) * mm});
            skLineSegment(sketch, "E33.0.6.13", {"start": v(35.2, 23.73) * mm, "end": v(42.7, 23.73) * mm});
            skLineSegment(sketch, "E33.0.6.14", {"start": v(29.71, 31.22) * mm, "end": v(22.21, 31.22) * mm});
            skLineSegment(sketch, "E33.0.6.15", {"start": v(12.98, 30.22) * mm, "end": v(25.96, 37.72) * mm, "construction": true});
            skCircle(sketch, "E33.0.6.16", {"center": v(0, 37.72) * mm, "radius": 7.5 * mm, "construction": true});
            skCircle(sketch, "E33.0.6.17", {"center": v(-12.98, 30.22) * mm, "radius": 7.5 * mm, "construction": true});
            skLineSegment(sketch, "E33.0.6.18", {"start": v(-16.73, 36.72) * mm, "end": v(-9.23, 36.72) * mm});
            skLineSegment(sketch, "E33.0.6.19", {"start": v(-3.75, 31.22) * mm, "end": v(-7.5, 37.72) * mm});
            skLineSegment(sketch, "E33.0.6.20", {"start": v(3.75, 44.21) * mm, "end": v(7.5, 37.72) * mm});
            skLineSegment(sketch, "E33.0.6.21", {"start": v(-22.21, 31.22) * mm, "end": v(-18.46, 37.72) * mm});
            skLineSegment(sketch, "E33.0.6.22", {"start": v(-31.45, 30.22) * mm, "end": v(-35.2, 23.73) * mm});
            skLineSegment(sketch, "E33.0.6.23", {"start": v(16.73, 36.72) * mm, "end": v(9.23, 36.72) * mm});
            skLineSegment(sketch, "E33.0.6.24", {"start": v(29.71, 44.21) * mm, "end": v(33.46, 37.72) * mm});
            skLineSegment(sketch, "E33.0.6.25", {"start": v(46.45, 30.22) * mm, "end": v(42.7, 36.72) * mm});
            skLineSegment(sketch, "E33.0.6.26", {"start": v(42.7, 23.73) * mm, "end": v(46.45, 30.22) * mm});
            skLineSegment(sketch, "E33.0.6.27", {"start": v(5.48, 30.22) * mm, "end": v(9.23, 23.73) * mm});
            skLineSegment(sketch, "E33.0.6.28", {"start": v(-46.45, 30.22) * mm, "end": v(-42.7, 36.72) * mm});
            skLineSegment(sketch, "E33.0.6.29", {"start": v(31.45, 30.22) * mm, "end": v(35.2, 23.73) * mm});
            skLineSegment(sketch, "E33.0.6.30", {"start": v(16.73, 23.73) * mm, "end": v(20.48, 30.22) * mm});
            skLineSegment(sketch, "E33.0.6.31", {"start": v(-16.73, 23.73) * mm, "end": v(-20.48, 30.22) * mm});
            skLineSegment(sketch, "E33.0.6.32", {"start": v(-29.71, 31.22) * mm, "end": v(-22.21, 31.22) * mm});
            skLineSegment(sketch, "E33.0.6.33", {"start": v(20.48, 30.22) * mm, "end": v(16.73, 36.72) * mm});
            skLineSegment(sketch, "E33.0.6.34", {"start": v(-12.98, 30.22) * mm, "end": v(-25.96, 37.72) * mm, "construction": true});
            skLineSegment(sketch, "E33.0.6.35", {"start": v(-18.46, 37.72) * mm, "end": v(-22.21, 44.21) * mm});
            skLineSegment(sketch, "E33.0.6.36", {"start": v(42.7, 36.72) * mm, "end": v(35.2, 36.72) * mm});
            skLineSegment(sketch, "E33.0.6.37", {"start": v(-22.21, 44.21) * mm, "end": v(-29.71, 44.21) * mm});
            skLineSegment(sketch, "E33.0.6.38", {"start": v(-35.2, 36.72) * mm, "end": v(-31.45, 30.22) * mm});
            skLineSegment(sketch, "E33.0.6.39", {"start": v(-9.23, 23.73) * mm, "end": v(-16.73, 23.73) * mm});
            skLineSegment(sketch, "E33.0.6.40", {"start": v(22.21, 44.21) * mm, "end": v(29.71, 44.21) * mm});
            skLineSegment(sketch, "E33.0.6.41", {"start": v(22.21, 31.22) * mm, "end": v(18.46, 37.72) * mm});
            skLineSegment(sketch, "E33.0.6.42", {"start": v(3.75, 31.22) * mm, "end": v(-3.75, 31.22) * mm});
            skLineSegment(sketch, "E33.0.6.43", {"start": v(38.95, 30.22) * mm, "end": v(25.96, 37.72) * mm, "construction": true});
            skCircle(sketch, "E33.0.6.44", {"center": v(12.98, 30.22) * mm, "radius": 7.5 * mm, "construction": true});
            skLineSegment(sketch, "E33.0.6.45", {"start": v(-29.71, 44.21) * mm, "end": v(-33.46, 37.72) * mm});
            skCircle(sketch, "E33.0.6.46", {"center": v(25.96, 37.72) * mm, "radius": 7.5 * mm, "construction": true});
            skLineSegment(sketch, "E33.0.6.47", {"start": v(18.46, 37.72) * mm, "end": v(22.21, 44.21) * mm});
            skLineSegment(sketch, "E33.0.6.48", {"start": v(-35.2, 23.73) * mm, "end": v(-42.7, 23.73) * mm});
            skLineSegment(sketch, "E33.0.6.49", {"start": v(9.23, 23.73) * mm, "end": v(16.73, 23.73) * mm});
            skLineSegment(sketch, "E33.0.6.50", {"start": v(-33.46, 37.72) * mm, "end": v(-29.71, 31.22) * mm});
            skLineSegment(sketch, "E33.0.6.51", {"start": v(-42.7, 36.72) * mm, "end": v(-35.2, 36.72) * mm});
            skLineSegment(sketch, "E33.0.6.52", {"start": v(-42.7, 23.73) * mm, "end": v(-46.45, 30.22) * mm});
            skLineSegment(sketch, "E33.0.6.53", {"start": v(-38.95, 30.22) * mm, "end": v(-25.96, 37.72) * mm, "construction": true});
            skLineSegment(sketch, "E33.0.6.54", {"start": v(-12.98, 30.22) * mm, "end": v(12.98, 30.22) * mm, "construction": true});
            skLineSegment(sketch, "E33.0.6.55", {"start": v(-9.23, 36.72) * mm, "end": v(-5.48, 30.22) * mm});
            skLineSegment(sketch, "E33.0.7.0", {"start": v(-3.75, 59.2) * mm, "end": v(3.75, 59.2) * mm});
            skLineSegment(sketch, "E33.0.7.1", {"start": v(-7.5, 52.7) * mm, "end": v(-3.75, 59.2) * mm});
            skLineSegment(sketch, "E33.0.7.2", {"start": v(7.5, 52.7) * mm, "end": v(3.75, 46.21) * mm});
            skLineSegment(sketch, "E33.0.7.3", {"start": v(-20.48, 45.21) * mm, "end": v(-16.73, 51.7) * mm});
            skCircle(sketch, "E33.0.7.4", {"center": v(-25.96, 52.7) * mm, "radius": 7.5 * mm, "construction": true});
            skLineSegment(sketch, "E33.0.7.5", {"start": v(35.2, 51.7) * mm, "end": v(31.45, 45.21) * mm});
            skLineSegment(sketch, "E33.0.7.6", {"start": v(12.98, 45.21) * mm, "end": v(0, 52.7) * mm, "construction": true});
            skCircle(sketch, "E33.0.7.7", {"center": v(38.95, 45.21) * mm, "radius": 7.5 * mm, "construction": true});
            skLineSegment(sketch, "E33.0.7.8", {"start": v(-12.98, 45.21) * mm, "end": v(0, 52.7) * mm, "construction": true});
            skLineSegment(sketch, "E33.0.7.9", {"start": v(9.23, 51.7) * mm, "end": v(5.48, 45.21) * mm});
            skCircle(sketch, "E33.0.7.10", {"center": v(-38.95, 45.21) * mm, "radius": 7.5 * mm, "construction": true});
            skLineSegment(sketch, "E33.0.7.11", {"start": v(-5.48, 45.21) * mm, "end": v(-9.23, 38.72) * mm});
            skLineSegment(sketch, "E33.0.7.12", {"start": v(33.46, 52.7) * mm, "end": v(29.71, 46.21) * mm});
            skLineSegment(sketch, "E33.0.7.13", {"start": v(35.2, 38.72) * mm, "end": v(42.7, 38.72) * mm});
            skLineSegment(sketch, "E33.0.7.14", {"start": v(29.71, 46.21) * mm, "end": v(22.21, 46.21) * mm});
            skLineSegment(sketch, "E33.0.7.15", {"start": v(12.98, 45.21) * mm, "end": v(25.96, 52.7) * mm, "construction": true});
            skCircle(sketch, "E33.0.7.16", {"center": v(0, 52.7) * mm, "radius": 7.5 * mm, "construction": true});
            skCircle(sketch, "E33.0.7.17", {"center": v(-12.98, 45.21) * mm, "radius": 7.5 * mm, "construction": true});
            skLineSegment(sketch, "E33.0.7.18", {"start": v(-16.73, 51.7) * mm, "end": v(-9.23, 51.7) * mm});
            skLineSegment(sketch, "E33.0.7.19", {"start": v(-3.75, 46.21) * mm, "end": v(-7.5, 52.7) * mm});
            skLineSegment(sketch, "E33.0.7.20", {"start": v(3.75, 59.2) * mm, "end": v(7.5, 52.7) * mm});
            skLineSegment(sketch, "E33.0.7.21", {"start": v(-22.21, 46.21) * mm, "end": v(-18.46, 52.7) * mm});
            skLineSegment(sketch, "E33.0.7.22", {"start": v(-31.45, 45.21) * mm, "end": v(-35.2, 38.72) * mm});
            skLineSegment(sketch, "E33.0.7.23", {"start": v(16.73, 51.7) * mm, "end": v(9.23, 51.7) * mm});
            skLineSegment(sketch, "E33.0.7.24", {"start": v(29.71, 59.2) * mm, "end": v(33.46, 52.7) * mm});
            skLineSegment(sketch, "E33.0.7.25", {"start": v(46.45, 45.21) * mm, "end": v(42.7, 51.7) * mm});
            skLineSegment(sketch, "E33.0.7.26", {"start": v(42.7, 38.72) * mm, "end": v(46.45, 45.21) * mm});
            skLineSegment(sketch, "E33.0.7.27", {"start": v(5.48, 45.21) * mm, "end": v(9.23, 38.72) * mm});
            skLineSegment(sketch, "E33.0.7.28", {"start": v(-46.45, 45.21) * mm, "end": v(-42.7, 51.7) * mm});
            skLineSegment(sketch, "E33.0.7.29", {"start": v(31.45, 45.21) * mm, "end": v(35.2, 38.72) * mm});
            skLineSegment(sketch, "E33.0.7.30", {"start": v(16.73, 38.72) * mm, "end": v(20.48, 45.21) * mm});
            skLineSegment(sketch, "E33.0.7.31", {"start": v(-16.73, 38.72) * mm, "end": v(-20.48, 45.21) * mm});
            skLineSegment(sketch, "E33.0.7.32", {"start": v(-29.71, 46.21) * mm, "end": v(-22.21, 46.21) * mm});
            skLineSegment(sketch, "E33.0.7.33", {"start": v(20.48, 45.21) * mm, "end": v(16.73, 51.7) * mm});
            skLineSegment(sketch, "E33.0.7.34", {"start": v(-12.98, 45.21) * mm, "end": v(-25.96, 52.7) * mm, "construction": true});
            skLineSegment(sketch, "E33.0.7.35", {"start": v(-18.46, 52.7) * mm, "end": v(-22.21, 59.2) * mm});
            skLineSegment(sketch, "E33.0.7.36", {"start": v(42.7, 51.7) * mm, "end": v(35.2, 51.7) * mm});
            skLineSegment(sketch, "E33.0.7.37", {"start": v(-22.21, 59.2) * mm, "end": v(-29.71, 59.2) * mm});
            skLineSegment(sketch, "E33.0.7.38", {"start": v(-35.2, 51.7) * mm, "end": v(-31.45, 45.21) * mm});
            skLineSegment(sketch, "E33.0.7.39", {"start": v(-9.23, 38.72) * mm, "end": v(-16.73, 38.72) * mm});
            skLineSegment(sketch, "E33.0.7.40", {"start": v(22.21, 59.2) * mm, "end": v(29.71, 59.2) * mm});
            skLineSegment(sketch, "E33.0.7.41", {"start": v(22.21, 46.21) * mm, "end": v(18.46, 52.7) * mm});
            skLineSegment(sketch, "E33.0.7.42", {"start": v(3.75, 46.21) * mm, "end": v(-3.75, 46.21) * mm});
            skLineSegment(sketch, "E33.0.7.43", {"start": v(38.95, 45.21) * mm, "end": v(25.96, 52.7) * mm, "construction": true});
            skCircle(sketch, "E33.0.7.44", {"center": v(12.98, 45.21) * mm, "radius": 7.5 * mm, "construction": true});
            skLineSegment(sketch, "E33.0.7.45", {"start": v(-29.71, 59.2) * mm, "end": v(-33.46, 52.7) * mm});
            skCircle(sketch, "E33.0.7.46", {"center": v(25.96, 52.7) * mm, "radius": 7.5 * mm, "construction": true});
            skLineSegment(sketch, "E33.0.7.47", {"start": v(18.46, 52.7) * mm, "end": v(22.21, 59.2) * mm});
            skLineSegment(sketch, "E33.0.7.48", {"start": v(-35.2, 38.72) * mm, "end": v(-42.7, 38.72) * mm});
            skLineSegment(sketch, "E33.0.7.49", {"start": v(9.23, 38.72) * mm, "end": v(16.73, 38.72) * mm});
            skLineSegment(sketch, "E33.0.7.50", {"start": v(-33.46, 52.7) * mm, "end": v(-29.71, 46.21) * mm});
            skLineSegment(sketch, "E33.0.7.51", {"start": v(-42.7, 51.7) * mm, "end": v(-35.2, 51.7) * mm});
            skLineSegment(sketch, "E33.0.7.52", {"start": v(-42.7, 38.72) * mm, "end": v(-46.45, 45.21) * mm});
            skLineSegment(sketch, "E33.0.7.53", {"start": v(-38.95, 45.21) * mm, "end": v(-25.96, 52.7) * mm, "construction": true});
            skLineSegment(sketch, "E33.0.7.54", {"start": v(-12.98, 45.21) * mm, "end": v(12.98, 45.21) * mm, "construction": true});
            skLineSegment(sketch, "E33.0.7.55", {"start": v(-9.23, 51.7) * mm, "end": v(-5.48, 45.21) * mm});
            skLineSegment(sketch, "E33.0.8.0", {"start": v(-3.75, 74.2) * mm, "end": v(3.75, 74.2) * mm});
            skLineSegment(sketch, "E33.0.8.1", {"start": v(-7.5, 67.7) * mm, "end": v(-3.75, 74.2) * mm});
            skLineSegment(sketch, "E33.0.8.2", {"start": v(7.5, 67.7) * mm, "end": v(3.75, 61.2) * mm});
            skLineSegment(sketch, "E33.0.8.3", {"start": v(-20.48, 60.2) * mm, "end": v(-16.73, 66.7) * mm});
            skCircle(sketch, "E33.0.8.4", {"center": v(-25.96, 67.7) * mm, "radius": 7.5 * mm, "construction": true});
            skLineSegment(sketch, "E33.0.8.5", {"start": v(35.2, 66.7) * mm, "end": v(31.45, 60.2) * mm});
            skLineSegment(sketch, "E33.0.8.6", {"start": v(12.98, 60.2) * mm, "end": v(0, 67.7) * mm, "construction": true});
            skCircle(sketch, "E33.0.8.7", {"center": v(38.95, 60.2) * mm, "radius": 7.5 * mm, "construction": true});
            skLineSegment(sketch, "E33.0.8.8", {"start": v(-12.98, 60.2) * mm, "end": v(0, 67.7) * mm, "construction": true});
            skLineSegment(sketch, "E33.0.8.9", {"start": v(9.23, 66.7) * mm, "end": v(5.48, 60.2) * mm});
            skCircle(sketch, "E33.0.8.10", {"center": v(-38.95, 60.2) * mm, "radius": 7.5 * mm, "construction": true});
            skLineSegment(sketch, "E33.0.8.11", {"start": v(-5.48, 60.2) * mm, "end": v(-9.23, 53.7) * mm});
            skLineSegment(sketch, "E33.0.8.12", {"start": v(33.46, 67.7) * mm, "end": v(29.71, 61.2) * mm});
            skLineSegment(sketch, "E33.0.8.13", {"start": v(35.2, 53.7) * mm, "end": v(42.7, 53.7) * mm});
            skLineSegment(sketch, "E33.0.8.14", {"start": v(29.71, 61.2) * mm, "end": v(22.21, 61.2) * mm});
            skLineSegment(sketch, "E33.0.8.15", {"start": v(12.98, 60.2) * mm, "end": v(25.96, 67.7) * mm, "construction": true});
            skCircle(sketch, "E33.0.8.16", {"center": v(0, 67.7) * mm, "radius": 7.5 * mm, "construction": true});
            skCircle(sketch, "E33.0.8.17", {"center": v(-12.98, 60.2) * mm, "radius": 7.5 * mm, "construction": true});
            skLineSegment(sketch, "E33.0.8.18", {"start": v(-16.73, 66.7) * mm, "end": v(-9.23, 66.7) * mm});
            skLineSegment(sketch, "E33.0.8.19", {"start": v(-3.75, 61.2) * mm, "end": v(-7.5, 67.7) * mm});
            skLineSegment(sketch, "E33.0.8.20", {"start": v(3.75, 74.2) * mm, "end": v(7.5, 67.7) * mm});
            skLineSegment(sketch, "E33.0.8.21", {"start": v(-22.21, 61.2) * mm, "end": v(-18.46, 67.7) * mm});
            skLineSegment(sketch, "E33.0.8.22", {"start": v(-31.45, 60.2) * mm, "end": v(-35.2, 53.7) * mm});
            skLineSegment(sketch, "E33.0.8.23", {"start": v(16.73, 66.7) * mm, "end": v(9.23, 66.7) * mm});
            skLineSegment(sketch, "E33.0.8.24", {"start": v(29.71, 74.2) * mm, "end": v(33.46, 67.7) * mm});
            skLineSegment(sketch, "E33.0.8.25", {"start": v(46.45, 60.2) * mm, "end": v(42.7, 66.7) * mm});
            skLineSegment(sketch, "E33.0.8.26", {"start": v(42.7, 53.7) * mm, "end": v(46.45, 60.2) * mm});
            skLineSegment(sketch, "E33.0.8.27", {"start": v(5.48, 60.2) * mm, "end": v(9.23, 53.7) * mm});
            skLineSegment(sketch, "E33.0.8.28", {"start": v(-46.45, 60.2) * mm, "end": v(-42.7, 66.7) * mm});
            skLineSegment(sketch, "E33.0.8.29", {"start": v(31.45, 60.2) * mm, "end": v(35.2, 53.7) * mm});
            skLineSegment(sketch, "E33.0.8.30", {"start": v(16.73, 53.7) * mm, "end": v(20.48, 60.2) * mm});
            skLineSegment(sketch, "E33.0.8.31", {"start": v(-16.73, 53.7) * mm, "end": v(-20.48, 60.2) * mm});
            skLineSegment(sketch, "E33.0.8.32", {"start": v(-29.71, 61.2) * mm, "end": v(-22.21, 61.2) * mm});
            skLineSegment(sketch, "E33.0.8.33", {"start": v(20.48, 60.2) * mm, "end": v(16.73, 66.7) * mm});
            skLineSegment(sketch, "E33.0.8.34", {"start": v(-12.98, 60.2) * mm, "end": v(-25.96, 67.7) * mm, "construction": true});
            skLineSegment(sketch, "E33.0.8.35", {"start": v(-18.46, 67.7) * mm, "end": v(-22.21, 74.2) * mm});
            skLineSegment(sketch, "E33.0.8.36", {"start": v(42.7, 66.7) * mm, "end": v(35.2, 66.7) * mm});
            skLineSegment(sketch, "E33.0.8.37", {"start": v(-22.21, 74.2) * mm, "end": v(-29.71, 74.2) * mm});
            skLineSegment(sketch, "E33.0.8.38", {"start": v(-35.2, 66.7) * mm, "end": v(-31.45, 60.2) * mm});
            skLineSegment(sketch, "E33.0.8.39", {"start": v(-9.23, 53.7) * mm, "end": v(-16.73, 53.7) * mm});
            skLineSegment(sketch, "E33.0.8.40", {"start": v(22.21, 74.2) * mm, "end": v(29.71, 74.2) * mm});
            skLineSegment(sketch, "E33.0.8.41", {"start": v(22.21, 61.2) * mm, "end": v(18.46, 67.7) * mm});
            skLineSegment(sketch, "E33.0.8.42", {"start": v(3.75, 61.2) * mm, "end": v(-3.75, 61.2) * mm});
            skLineSegment(sketch, "E33.0.8.43", {"start": v(38.95, 60.2) * mm, "end": v(25.96, 67.7) * mm, "construction": true});
            skCircle(sketch, "E33.0.8.44", {"center": v(12.98, 60.2) * mm, "radius": 7.5 * mm, "construction": true});
            skLineSegment(sketch, "E33.0.8.45", {"start": v(-29.71, 74.2) * mm, "end": v(-33.46, 67.7) * mm});
            skCircle(sketch, "E33.0.8.46", {"center": v(25.96, 67.7) * mm, "radius": 7.5 * mm, "construction": true});
            skLineSegment(sketch, "E33.0.8.47", {"start": v(18.46, 67.7) * mm, "end": v(22.21, 74.2) * mm});
            skLineSegment(sketch, "E33.0.8.48", {"start": v(-35.2, 53.7) * mm, "end": v(-42.7, 53.7) * mm});
            skLineSegment(sketch, "E33.0.8.49", {"start": v(9.23, 53.7) * mm, "end": v(16.73, 53.7) * mm});
            skLineSegment(sketch, "E33.0.8.50", {"start": v(-33.46, 67.7) * mm, "end": v(-29.71, 61.2) * mm});
            skLineSegment(sketch, "E33.0.8.51", {"start": v(-42.7, 66.7) * mm, "end": v(-35.2, 66.7) * mm});
            skLineSegment(sketch, "E33.0.8.52", {"start": v(-42.7, 53.7) * mm, "end": v(-46.45, 60.2) * mm});
            skLineSegment(sketch, "E33.0.8.53", {"start": v(-38.95, 60.2) * mm, "end": v(-25.96, 67.7) * mm, "construction": true});
            skLineSegment(sketch, "E33.0.8.54", {"start": v(-12.98, 60.2) * mm, "end": v(12.98, 60.2) * mm, "construction": true});
            skLineSegment(sketch, "E33.0.8.55", {"start": v(-9.23, 66.7) * mm, "end": v(-5.48, 60.2) * mm});
            skLineSegment(sketch, "E33.direction1", {"start": v(-42.7, -66.21) * mm, "end": v(-40, -66.21) * mm, "construction": true});
            skLineSegment(sketch, "E33.direction2", {"start": v(-42.7, -66.21) * mm, "end": v(-42.7, -51.22) * mm, "construction": true});
            skSolve(sketch);
        }
        {
            var Q0;
            Q0 = qSketchRegion(id + "F2", true);
            extrude(context, id + "F3", {"entities" : qUnion([Q0]), "operationType" : NewBodyOperationType.REMOVE, "depth" : 25 * mm});
        }
        {
            var Q0;
            Q0 = qSketchRegion(id + "F0", true);
            extrude(context, id + "F4", {"entities" : qUnion([Q0]), "depth" : 20 * mm});
        }
        {
            var Q0;
            Q0=makeQuery(id+"F4.opExtrude","CAP_FACE",FACE,{"disambiguationData":[OSD([sQuery(id+"F0.wireOp",EDGE,"E0.bottom"),sQuery(id+"F0.wireOp",EDGE,"E0.top"),sQuery(id+"F0.wireOp",EDGE,"E0.left"),sQuery(id+"F0.wireOp",EDGE,"E0.right"),sQuery(id+"F0.wireOp",EDGE,"E1"),sQuery(id+"F0.wireOp",EDGE,"E2"),sQuery(id+"F0.wireOp",EDGE,"E3"),sQuery(id+"F0.wireOp",EDGE,"E4")])],"isStart":false});
            var Q1;
            Q1=makeQuery(id+"F4.opExtrude","CAP_FACE",FACE,{"disambiguationData":[OSD([sQuery(id+"F0.wireOp",EDGE,"E0.bottom"),sQuery(id+"F0.wireOp",EDGE,"E0.top"),sQuery(id+"F0.wireOp",EDGE,"E0.left"),sQuery(id+"F0.wireOp",EDGE,"E0.right"),sQuery(id+"F0.wireOp",EDGE,"E1"),sQuery(id+"F0.wireOp",EDGE,"E2"),sQuery(id+"F0.wireOp",EDGE,"E3"),sQuery(id+"F0.wireOp",EDGE,"E4")])],"isStart":true});
            shell(context, id + "F5", {"entities" : qUnion([Q0, Q1]), "thickness" : 2.5 * mm});
        }
        {
            var Q0;
            Q0=qCreatedBy(makeId("Front.planeOp"),FACE);
            var sketch = newSketch(context, id + "F6", { "sketchPlane" : qUnion([Q0])});
            skCircle(sketch, "E34", {"center": v(0, 0) * mm, "radius": 1.5 * mm});
            skCircle(sketch, "E35", {"center": v(12.98, 0) * mm, "radius": 1.5 * mm});
            skCircle(sketch, "E36", {"center": v(-12.98, 0) * mm, "radius": 1.5 * mm});
            skCircle(sketch, "E37", {"center": v(-25.96, 0) * mm, "radius": 1.5 * mm});
            skCircle(sketch, "E38", {"center": v(25.96, 0) * mm, "radius": 1.5 * mm});
            skLineSegment(sketch, "E39", {"start": v(-25.96, 0) * mm, "end": v(-12.98, 0) * mm, "construction": true});
            skLineSegment(sketch, "E40", {"start": v(-12.98, 0) * mm, "end": v(0, 0) * mm, "construction": true});
            skLineSegment(sketch, "E41", {"start": v(0, 0) * mm, "end": v(12.98, 0) * mm, "construction": true});
            skLineSegment(sketch, "E42", {"start": v(12.98, 0) * mm, "end": v(25.96, 0) * mm, "construction": true});
            skSolve(sketch);
        }
        {
            var Q0;
            Q0 = qSketchRegion(id + "F6", true);
            extrude(context, id + "F7", {"entities" : qUnion([Q0]), "operationType" : NewBodyOperationType.REMOVE, "oppositeDirection" : true, "depth" : 80 * mm, "hasSecondDirection" : true, "secondDirectionOppositeDirection" : false, "secondDirectionDepth" : 80 * mm});
        }
        {
            var Q0;
            Q0=qCreatedBy(makeId("Right.planeOp"),FACE);
            var sketch = newSketch(context, id + "F8", { "sketchPlane" : qUnion([Q0])});
            skCircle(sketch, "E43", {"center": v(0, 0) * mm, "radius": 1.5 * mm});
            skCircle(sketch, "E44", {"center": v(-15, 0) * mm, "radius": 1.5 * mm});
            skCircle(sketch, "E45", {"center": v(-29.98, 0) * mm, "radius": 1.5 * mm});
            skCircle(sketch, "E46", {"center": v(-44.97, 0) * mm, "radius": 1.5 * mm});
            skCircle(sketch, "E47", {"center": v(15, 0) * mm, "radius": 1.5 * mm});
            skCircle(sketch, "E48", {"center": v(29.98, 0) * mm, "radius": 1.5 * mm});
            skCircle(sketch, "E49", {"center": v(44.97, 0) * mm, "radius": 1.5 * mm});
            skLineSegment(sketch, "E50", {"start": v(-44.97, 0) * mm, "end": v(-29.98, 0) * mm, "construction": true});
            skLineSegment(sketch, "E51", {"start": v(-29.98, 0) * mm, "end": v(-15, 0) * mm, "construction": true});
            skLineSegment(sketch, "E52", {"start": v(-15, 0) * mm, "end": v(0, 0) * mm, "construction": true});
            skLineSegment(sketch, "E53", {"start": v(0, 0) * mm, "end": v(15, 0) * mm, "construction": true});
            skLineSegment(sketch, "E54", {"start": v(15, 0) * mm, "end": v(29.98, 0) * mm, "construction": true});
            skLineSegment(sketch, "E55", {"start": v(29.98, 0) * mm, "end": v(44.97, 0) * mm, "construction": true});
            skSolve(sketch);
        }
        {
            var Q0;
            Q0 = qSketchRegion(id + "F8", true);
            extrude(context, id + "F9", {"entities" : qUnion([Q0]), "operationType" : NewBodyOperationType.REMOVE, "oppositeDirection" : true, "depth" : 60 * mm, "hasSecondDirection" : true, "secondDirectionOppositeDirection" : false, "secondDirectionDepth" : 60 * mm});
        }
    });
